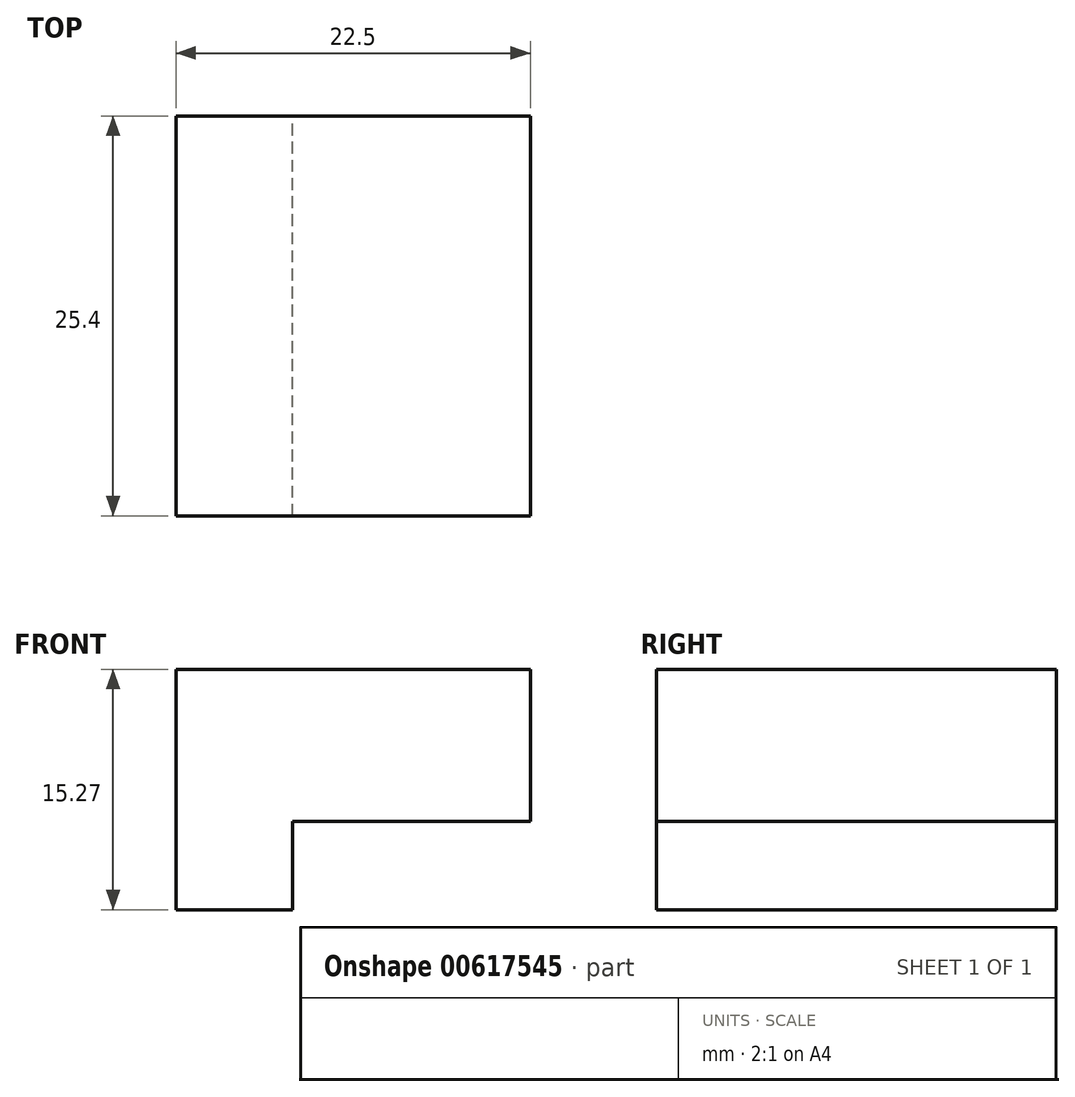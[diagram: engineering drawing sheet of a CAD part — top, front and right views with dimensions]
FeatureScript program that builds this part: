
annotation { "Feature Type Name" : "Feature", "Feature Type Description" : "" }
export const myFeature = defineFeature(function(context is Context, id is Id, definition is map)
    precondition{}
    {
        {
            var Q0;
            Q0=qCreatedBy(makeId("Front.planeOp"),FACE);
            var sketch = newSketch(context, id + "F0", { "sketchPlane" : qUnion([Q0])});
            skLineSegment(sketch, "E0", {"start": v(-7.4, 0) * mm, "end": v(-7.4, 15.27) * mm});
            skLineSegment(sketch, "E1", {"start": v(-7.4, 15.27) * mm, "end": v(15.1, 15.27) * mm});
            skLineSegment(sketch, "E2", {"start": v(15.1, 15.27) * mm, "end": v(15.1, 5.6) * mm});
            skLineSegment(sketch, "E3", {"start": v(-7.4, 0) * mm, "end": v(0, 0) * mm});
            skLineSegment(sketch, "E4", {"start": v(15.1, 5.6) * mm, "end": v(0, 5.6) * mm});
            skLineSegment(sketch, "E5", {"start": v(0, 5.6) * mm, "end": v(0, 0) * mm});
            skSolve(sketch);
        }
        {
            var Q0;
            Q0 = qSketchRegion(id + "F0", true);
            extrude(context, id + "F1", {"entities" : qUnion([Q0]), "depth" : 25.4 * mm, "offsetDistance" : 25.4 * mm});
        }
    });
